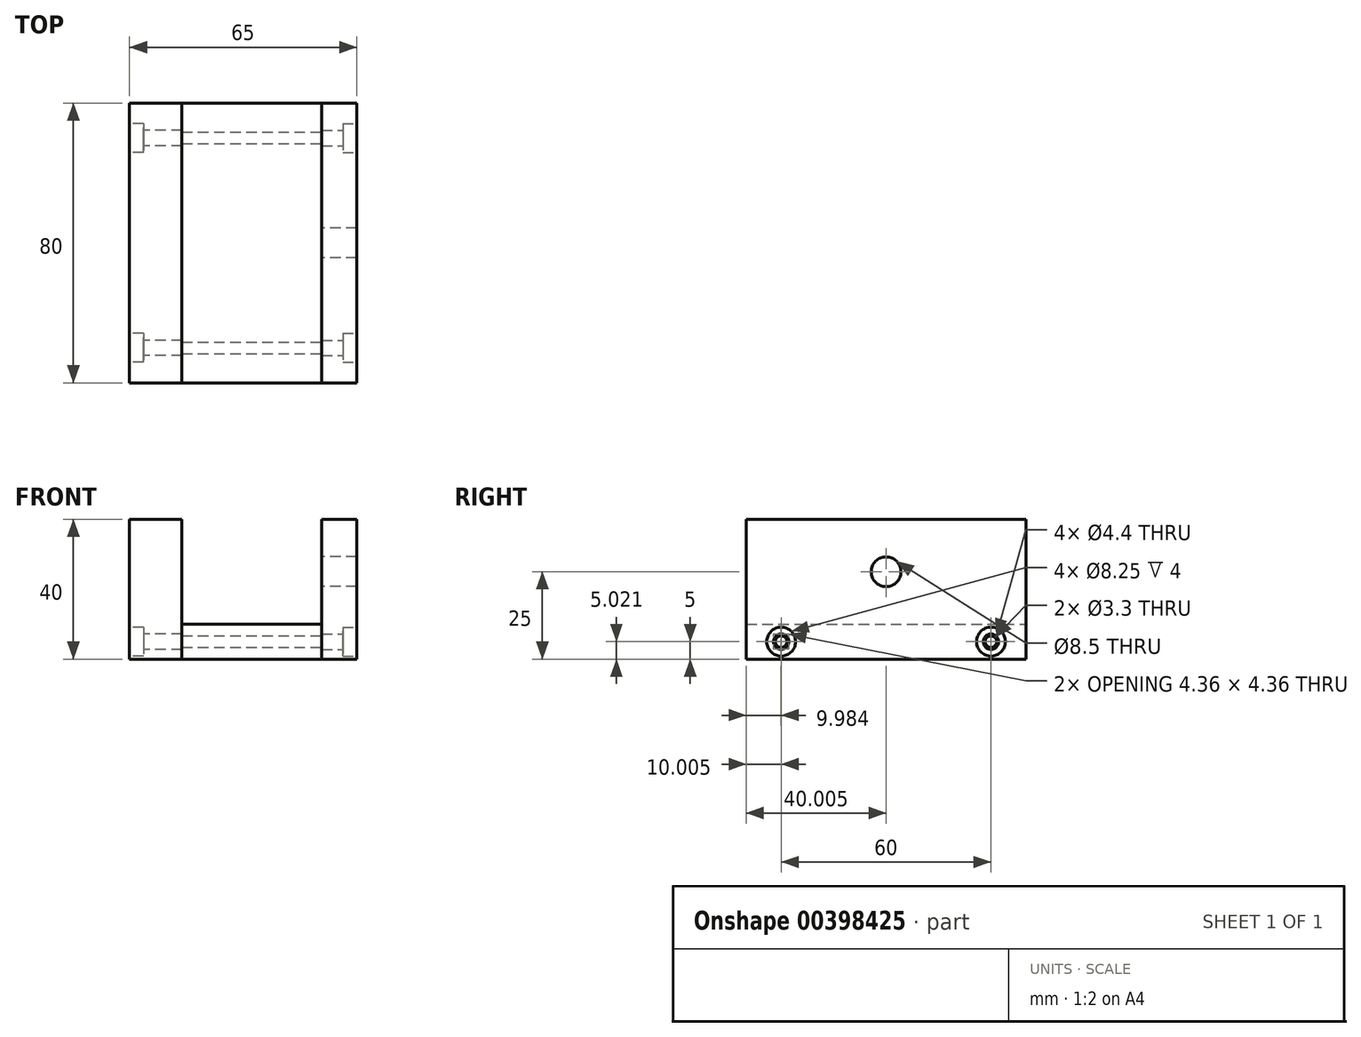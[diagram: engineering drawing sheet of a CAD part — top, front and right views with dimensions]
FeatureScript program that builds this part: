
annotation { "Feature Type Name" : "Feature", "Feature Type Description" : "" }
export const myFeature = defineFeature(function(context is Context, id is Id, definition is map)
    precondition{}
    {
        {
            var Q0;
            Q0=qCreatedBy(makeId("Top.planeOp"),FACE);
            var sketch = newSketch(context, id + "F0", { "sketchPlane" : qUnion([Q0])});
            skLineSegment(sketch, "E0.bottom", {"start": v(-42.83, -30.74) * mm, "end": v(-2.83, -30.74) * mm});
            skLineSegment(sketch, "E0.top", {"start": v(-42.83, 49.26) * mm, "end": v(-2.83, 49.26) * mm});
            skLineSegment(sketch, "E0.left", {"start": v(-42.83, -30.74) * mm, "end": v(-42.83, 49.26) * mm});
            skLineSegment(sketch, "E0.right", {"start": v(-2.83, -30.74) * mm, "end": v(-2.83, 49.26) * mm});
            skLineSegment(sketch, "E1.bottom", {"start": v(-2.83, 49.26) * mm, "end": v(7.17, 49.26) * mm});
            skLineSegment(sketch, "E1.top", {"start": v(-2.83, -30.74) * mm, "end": v(7.17, -30.74) * mm});
            skLineSegment(sketch, "E1.left", {"start": v(-2.83, 49.26) * mm, "end": v(-2.83, -30.74) * mm});
            skLineSegment(sketch, "E1.right", {"start": v(7.17, 49.26) * mm, "end": v(7.17, -30.74) * mm});
            skLineSegment(sketch, "E2.bottom", {"start": v(-42.83, 49.26) * mm, "end": v(-57.83, 49.26) * mm});
            skLineSegment(sketch, "E2.top", {"start": v(-42.83, -30.74) * mm, "end": v(-57.83, -30.74) * mm});
            skLineSegment(sketch, "E2.left", {"start": v(-42.83, 49.26) * mm, "end": v(-42.83, -30.74) * mm});
            skLineSegment(sketch, "E2.right", {"start": v(-57.83, 49.26) * mm, "end": v(-57.83, -30.74) * mm});
            skSolve(sketch);
        }
        {
            var Q0;
            Q0=makeQuery(id+"F0.imprint","IMPRINT",FACE,{"disambiguationData":[TD([[makeQuery(id+"F0.imprint","IMPRINT",EDGE,{"derivedFrom":sQuery(id+"F0.wireOp",EDGE,"E0.bottom")}),1.0]])]});
            extrude(context, id + "F1", {"entities" : qUnion([Q0]), "depth" : 10 * mm});
        }
        {
            var Q0;
            Q0=makeQuery(id+"F0.imprint","IMPRINT",FACE,{"disambiguationData":[TD([[makeQuery(id+"F0.imprint","IMPRINT",EDGE,{"derivedFrom":sQuery(id+"F0.wireOp",EDGE,"E2.bottom")}),1.0]])]});
            var Q1;
            Q1=makeQuery(id+"F0.imprint","IMPRINT",FACE,{"disambiguationData":[TD([[makeQuery(id+"F0.imprint","IMPRINT",EDGE,{"derivedFrom":sQuery(id+"F0.wireOp",EDGE,"E1.bottom")}),-1.0]])]});
            extrude(context, id + "F2", {"entities" : qUnion([Q0, Q1]), "depth" : 40 * mm});
        }
        {
            var Q0;
            Q0=makeQuery(id+"F2.opExtrude","SWEPT_FACE",FACE,{"disambiguationData":[OSD([sQuery(id+"F0.wireOp",EDGE,"E1.right")])]});
            var sketch = newSketch(context, id + "F3", { "sketchPlane" : qUnion([Q0])});
            skPoint(sketch, "E3", {"position": v(39.26, 5) * mm});
            skPoint(sketch, "E4", {"position": v(-20.74, 5) * mm});
            skSolve(sketch);
        }
        {
            var Q0;
            Q0=sQuery(id+"F3.wireOp",VERTEX,"E4");
            var Q1;
            Q1=sQuery(id+"F3.wireOp",VERTEX,"E3");
            var Q2;
            Q2=makeQuery(id+"F2.opExtrude","SWEPT_BODY",BODY,{"disambiguationData":[OSD([sQuery(id+"F0.wireOp",EDGE,"E1.bottom"),sQuery(id+"F0.wireOp",EDGE,"E1.top"),sQuery(id+"F0.wireOp",EDGE,"E1.left"),sQuery(id+"F0.wireOp",EDGE,"E1.right")])]});
            hole(context, id + "F4", {"style" : HoleStyle.C_BORE, "endStyle" : HoleEndStyle.THROUGH, "standardTappedOrClearance" : lookupTablePath({ "standard" : "ISO", "fit" : "Normal", "size" : "M4", "type" : "Clearance" }), "standardBlindInLast" : lookupTablePath({ "fit" : "Standard", "standard" : "ISO", "size" : "M4", "type" : "Clearance" }), "holeDiameter" : 4.4 * mm, "cBoreDiameter" : 8.25 * mm, "cBoreDepth" : 4 * mm, "isTappedThrough" : true, "tappedDepth" : 12 * mm, "tapClearance" : 3, "locations" : qUnion([Q0, Q1]), "scope" : qUnion([Q2])});
        }
        {
            var Q0;
            Q0=sQuery(id+"F3.wireOp",VERTEX,"E4");
            var Q1;
            Q1=sQuery(id+"F3.wireOp",VERTEX,"E3");
            var Q2;
            Q2=makeQuery(id+"F1.opExtrude","SWEPT_BODY",BODY,{"disambiguationData":[OSD([sQuery(id+"F0.wireOp",EDGE,"E0.bottom"),sQuery(id+"F0.wireOp",EDGE,"E0.top"),sQuery(id+"F0.wireOp",EDGE,"E1.left"),sQuery(id+"F0.wireOp",EDGE,"E2.left")])]});
            hole(context, id + "F5", {"style" : HoleStyle.SIMPLE, "endStyle" : HoleEndStyle.BLIND, "standardTappedOrClearance" : lookupTablePath({ "standard" : "ISO", "engagement" : "75%", "pitch" : "0.7 mm", "size" : "M4", "type" : "Tapped" }), "standardBlindInLast" : lookupTablePath({ "standard" : "ISO", "engagement" : "75%", "pitch" : "0.7 mm", "size" : "M4", "type" : "Tapped" }), "holeDiameter" : 3.3 * mm, "showTappedDepth" : true, "holeDepth" : 20 * mm, "isTappedThrough" : true, "tappedDepth" : 17.9 * mm, "tapClearance" : 3, "locations" : qUnion([Q0, Q1]), "scope" : qUnion([Q2]), "majorDiameter" : 4 * mm});
        }
        {
            var Q0;
            Q0=makeQuery(id+"F2.opExtrude","SWEPT_FACE",FACE,{"disambiguationData":[OSD([sQuery(id+"F0.wireOp",EDGE,"E2.right")])]});
            var sketch = newSketch(context, id + "F6", { "sketchPlane" : qUnion([Q0])});
            skPoint(sketch, "E5", {"position": v(20.74, 5) * mm});
            skPoint(sketch, "E6", {"position": v(-39.26, 5) * mm});
            skPoint(sketch, "E7", {"position": v(-9.26, 25) * mm});
            skSolve(sketch);
        }
        {
            var Q0;
            Q0=sQuery(id+"F6.wireOp",VERTEX,"E6");
            var Q1;
            Q1=sQuery(id+"F6.wireOp",VERTEX,"E5");
            var Q2;
            Q2=makeQuery(id+"F2.opExtrude","SWEPT_BODY",BODY,{"disambiguationData":[OSD([sQuery(id+"F0.wireOp",EDGE,"E2.bottom"),sQuery(id+"F0.wireOp",EDGE,"E2.top"),sQuery(id+"F0.wireOp",EDGE,"E2.left"),sQuery(id+"F0.wireOp",EDGE,"E2.right")])]});
            hole(context, id + "F7", {"style" : HoleStyle.C_BORE, "endStyle" : HoleEndStyle.THROUGH, "standardTappedOrClearance" : lookupTablePath({ "standard" : "ISO", "fit" : "Normal", "size" : "M4", "type" : "Clearance" }), "standardBlindInLast" : lookupTablePath({ "fit" : "Standard", "standard" : "ISO", "size" : "M4", "type" : "Clearance" }), "holeDiameter" : 4.4 * mm, "cBoreDiameter" : 8.25 * mm, "cBoreDepth" : 4 * mm, "isTappedThrough" : true, "tappedDepth" : 17.9 * mm, "tapClearance" : 3, "locations" : qUnion([Q0, Q1]), "scope" : qUnion([Q2])});
        }
        {
            var Q0;
            Q0=sQuery(id+"F6.wireOp",VERTEX,"E6");
            var Q1;
            Q1=sQuery(id+"F6.wireOp",VERTEX,"E5");
            var Q2;
            Q2=makeQuery(id+"F1.opExtrude","SWEPT_BODY",BODY,{"disambiguationData":[OSD([sQuery(id+"F0.wireOp",EDGE,"E0.bottom"),sQuery(id+"F0.wireOp",EDGE,"E0.top"),sQuery(id+"F0.wireOp",EDGE,"E1.left"),sQuery(id+"F0.wireOp",EDGE,"E2.left")])]});
            hole(context, id + "F8", {"style" : HoleStyle.SIMPLE, "endStyle" : HoleEndStyle.BLIND, "standardTappedOrClearance" : lookupTablePath({ "standard" : "ISO", "engagement" : "75%", "pitch" : "0.7 mm", "size" : "M4", "type" : "Tapped" }), "standardBlindInLast" : lookupTablePath({ "standard" : "ISO", "engagement" : "75%", "pitch" : "0.7 mm", "size" : "M4", "type" : "Tapped" }), "holeDiameter" : 3.3 * mm, "showTappedDepth" : true, "holeDepth" : 20 * mm, "isTappedThrough" : true, "tappedDepth" : 17.9 * mm, "tapClearance" : 3, "locations" : qUnion([Q0, Q1]), "scope" : qUnion([Q2]), "majorDiameter" : 4 * mm});
        }
        {
            var Q0;
            Q0=sQuery(id+"F6.wireOp",VERTEX,"E7");
            var Q1;
            Q1=makeQuery(id+"F2.opExtrude","SWEPT_BODY",BODY,{"disambiguationData":[OSD([sQuery(id+"F0.wireOp",EDGE,"E1.bottom"),sQuery(id+"F0.wireOp",EDGE,"E1.top"),sQuery(id+"F0.wireOp",EDGE,"E1.left"),sQuery(id+"F0.wireOp",EDGE,"E1.right")])]});
            hole(context, id + "F9", {"style" : HoleStyle.SIMPLE, "endStyle" : HoleEndStyle.THROUGH, "standardTappedOrClearance" : lookupTablePath({ "standard" : "ISO", "engagement" : "75%", "pitch" : "1.5 mm", "size" : "M10", "type" : "Tapped" }), "standardBlindInLast" : lookupTablePath({ "standard" : "ISO", "engagement" : "75%", "pitch" : "1.5 mm", "size" : "M10", "type" : "Tapped" }), "holeDiameter" : 8.5 * mm, "showTappedDepth" : true, "isTappedThrough" : true, "tappedDepth" : 17.9 * mm, "tapClearance" : 3, "locations" : qUnion([Q0]), "scope" : qUnion([Q1]), "majorDiameter" : 10 * mm});
        }
    });
